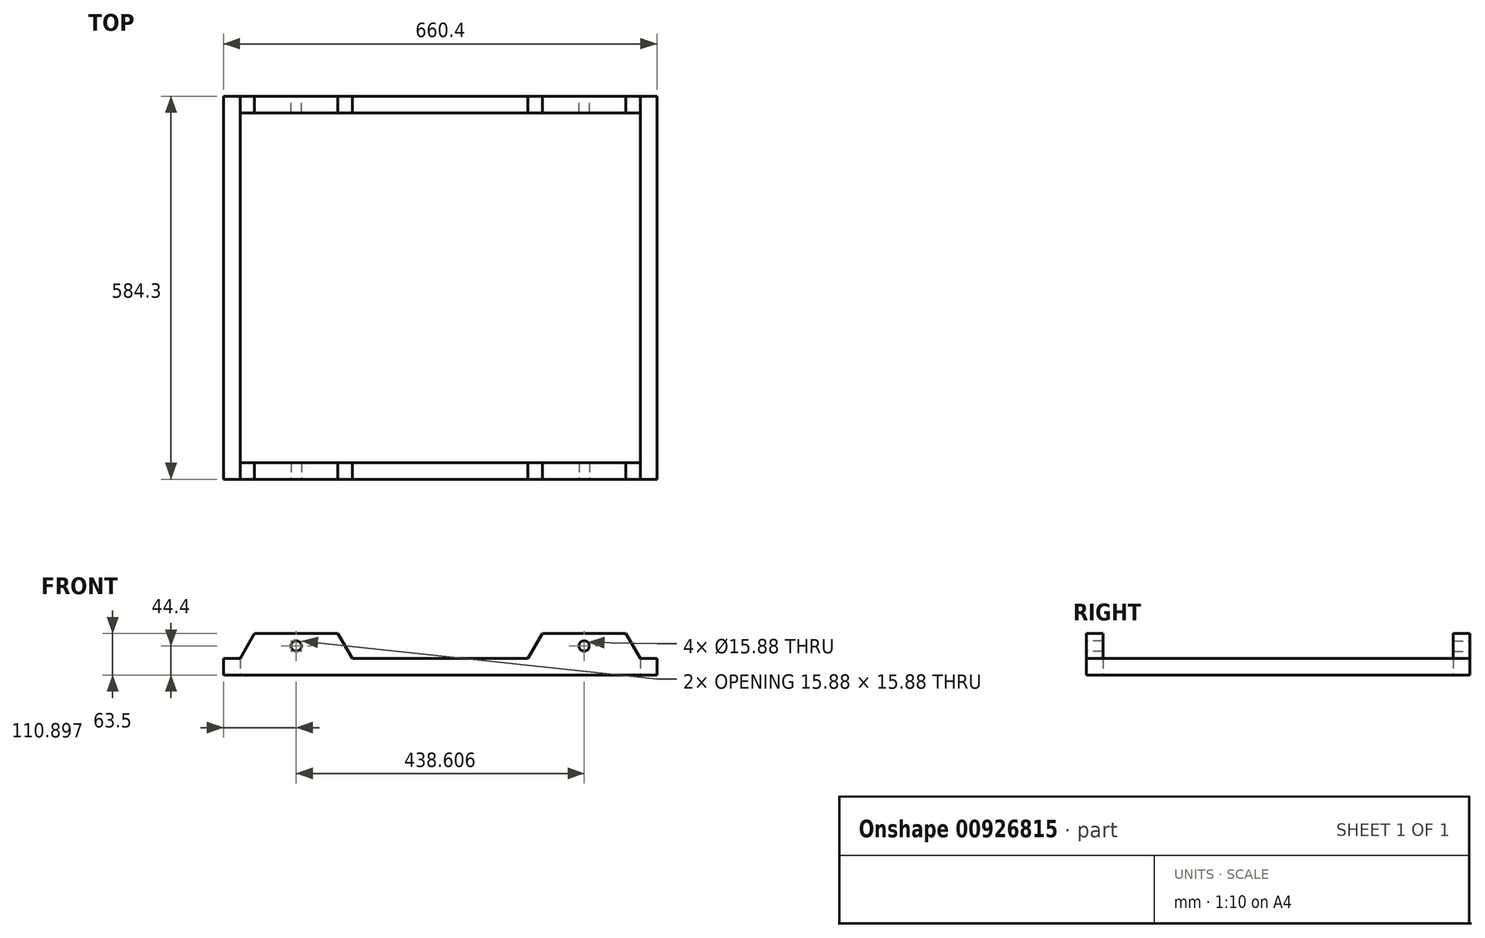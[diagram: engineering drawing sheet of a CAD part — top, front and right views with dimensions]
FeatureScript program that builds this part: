
annotation { "Feature Type Name" : "Feature", "Feature Type Description" : "" }
export const myFeature = defineFeature(function(context is Context, id is Id, definition is map)
    precondition{}
    {
        {
            var Q0;
            Q0=qCreatedBy(makeId("Top.planeOp"),FACE);
            var sketch = newSketch(context, id + "F0", { "sketchPlane" : qUnion([Q0])});
            skLineSegment(sketch, "E0.bottom", {"start": v(-304.8, 266.75) * mm, "end": v(304.8, 266.75) * mm, "construction": true});
            skLineSegment(sketch, "E0.top", {"start": v(-304.8, -266.75) * mm, "end": v(304.8, -266.75) * mm, "construction": true});
            skLineSegment(sketch, "E0.left", {"start": v(-304.8, 266.75) * mm, "end": v(-304.8, -266.75) * mm, "construction": true});
            skLineSegment(sketch, "E0.right", {"start": v(304.8, 266.75) * mm, "end": v(304.8, -266.75) * mm, "construction": true});
            skLineSegment(sketch, "E1", {"start": v(-304.8, -266.75) * mm, "end": v(-304.8, 266.75) * mm});
            skLineSegment(sketch, "E2", {"start": v(304.8, 266.75) * mm, "end": v(304.8, -266.75) * mm});
            skLineSegment(sketch, "E3", {"start": v(304.8, -266.75) * mm, "end": v(-304.8, -266.75) * mm});
            skLineSegment(sketch, "E4", {"start": v(-304.8, 266.75) * mm, "end": v(304.8, 266.75) * mm});
            skSolve(sketch);
        }
        {
            var Q0;
            Q0=qCreatedBy(makeId("Front.planeOp"),FACE);
            var sketch = newSketch(context, id + "F1", { "sketchPlane" : qUnion([Q0])});
            skLineSegment(sketch, "E5.bottom", {"start": v(-330.2, 12.7) * mm, "end": v(-304.8, 12.7) * mm});
            skLineSegment(sketch, "E5.top", {"start": v(-330.2, -12.7) * mm, "end": v(-304.8, -12.7) * mm});
            skLineSegment(sketch, "E5.left", {"start": v(-330.2, 12.7) * mm, "end": v(-330.2, -12.7) * mm});
            skLineSegment(sketch, "E5.right", {"start": v(-304.8, 12.7) * mm, "end": v(-304.8, -12.7) * mm});
            skSolve(sketch);
        }
        {
            var Q0;
            Q0=makeQuery(id+"F1.imprint","IMPRINT",FACE,{"disambiguationData":[TD([[makeQuery(id+"F1.imprint","IMPRINT",EDGE,{"derivedFrom":sQuery(id+"F1.wireOp",EDGE,"E5.bottom")}),-1.0]])]});
            var Q1;
            Q1=sQuery(id+"F0.wireOp",EDGE,"E1");
            var Q2;
            Q2=sQuery(id+"F0.wireOp",EDGE,"E4");
            var Q3;
            Q3=sQuery(id+"F0.wireOp",EDGE,"E2");
            var Q4;
            Q4=sQuery(id+"F0.wireOp",EDGE,"E3");
            sweep(context, id + "F2", {"profiles" : qUnion([Q0]), "path" : qUnion([Q1, Q2, Q3, Q4])});
        }
        {
            var Q0;
            Q0=makeQuery(id+"F2.opSweep","SWEPT_FACE",FACE,{"disambiguationData":[OSD([sQuery(id+"F0.wireOp",EDGE,"E3"),sQuery(id+"F1.wireOp",EDGE,"E5.left")])]});
            var sketch = newSketch(context, id + "F3", { "sketchPlane" : qUnion([Q0])});
            skLineSegment(sketch, "E6", {"start": v(304.8, 12.7) * mm, "end": v(282.8, 50.8) * mm});
            skLineSegment(sketch, "E7", {"start": v(282.8, 50.8) * mm, "end": v(155.8, 50.8) * mm});
            skLineSegment(sketch, "E8", {"start": v(155.8, 50.8) * mm, "end": v(133.8, 12.7) * mm});
            skLineSegment(sketch, "E9", {"start": v(133.8, 12.7) * mm, "end": v(304.8, 12.7) * mm});
            skPoint(sketch, "E10", {"position": v(219.3, 31.7) * mm});
            skSolve(sketch);
        }
        {
            var Q0;
            {var subQ0=sQuery(id+"F3.wireOp",EDGE,"E6");Q0=makeQuery(id+"F3.imprint","IMPRINT",FACE,{"disambiguationData":[TD([[makeQuery(id+"F3.imprint","IMPRINT",EDGE,{"derivedFrom":subQ0}),1.0]])]});}
            var Q1;
            Q1=makeQuery(id+"F2.opSweep","SWEPT_FACE",FACE,{"disambiguationData":[OSD([sQuery(id+"F0.wireOp",EDGE,"E3"),sQuery(id+"F1.wireOp",EDGE,"E5.right")])]});
            extrude(context, id + "F4", {"entities" : qUnion([Q0]), "endBound" : BoundingType.UP_TO_SURFACE, "oppositeDirection" : true, "depth" : 25 * mm, "endBoundEntityFace" : qUnion([Q1]), "offsetDistance" : 25 * mm});
        }
        {
            var Q0;
            Q0=sQuery(id+"F3.wireOp",VERTEX,"E10");
            var Q1;
            Q1=makeQuery(id+"F4.opExtrude","SWEPT_BODY",BODY,{"disambiguationData":[OSD([sQuery(id+"F3.wireOp",EDGE,"E6"),sQuery(id+"F3.wireOp",EDGE,"E7"),sQuery(id+"F3.wireOp",EDGE,"E8"),sQuery(id+"F3.wireOp",EDGE,"E9")])]});
            hole(context, id + "F5", {"style" : HoleStyle.SIMPLE, "endStyle" : HoleEndStyle.THROUGH, "holeDiameter" : 15.88 * mm, "majorDiameter" : 5 * mm, "isTappedThrough" : true, "tappedDepth" : 12 * mm, "tapClearance" : 3, "startFromSketch" : true, "locations" : qUnion([Q0]), "scope" : qUnion([Q1])});
        }
        {
            var Q0;
            Q0=makeQuery(id+"F4.opExtrude","SWEPT_BODY",BODY,{"disambiguationData":[OSD([sQuery(id+"F3.wireOp",EDGE,"E6"),sQuery(id+"F3.wireOp",EDGE,"E7"),sQuery(id+"F3.wireOp",EDGE,"E8"),sQuery(id+"F3.wireOp",EDGE,"E9")])]});
            var Q1;
            Q1=qCreatedBy(makeId("Right.planeOp"),FACE);
            mirror(context, id + "F6", {"entities" : qUnion([Q0]), "mirrorPlane" : qUnion([Q1])});
        }
        {
            var Q0;
            Q0=makeQuery(id+"F6.opPattern","COPY",BODY,{"derivedFrom":makeQuery(id+"F4.opExtrude","SWEPT_BODY",BODY,{"disambiguationData":[OSD([sQuery(id+"F3.wireOp",EDGE,"E6"),sQuery(id+"F3.wireOp",EDGE,"E7"),sQuery(id+"F3.wireOp",EDGE,"E8"),sQuery(id+"F3.wireOp",EDGE,"E9")])]}),"instanceName":"1"});
            var Q1;
            Q1=makeQuery(id+"F4.opExtrude","SWEPT_BODY",BODY,{"disambiguationData":[OSD([sQuery(id+"F3.wireOp",EDGE,"E6"),sQuery(id+"F3.wireOp",EDGE,"E7"),sQuery(id+"F3.wireOp",EDGE,"E8"),sQuery(id+"F3.wireOp",EDGE,"E9")])]});
            var Q2;
            Q2=qCreatedBy(makeId("Front.planeOp"),FACE);
            mirror(context, id + "F7", {"operationType" : NewBodyOperationType.ADD, "entities" : qUnion([Q0, Q1]), "mirrorPlane" : qUnion([Q2])});
        }
    });
